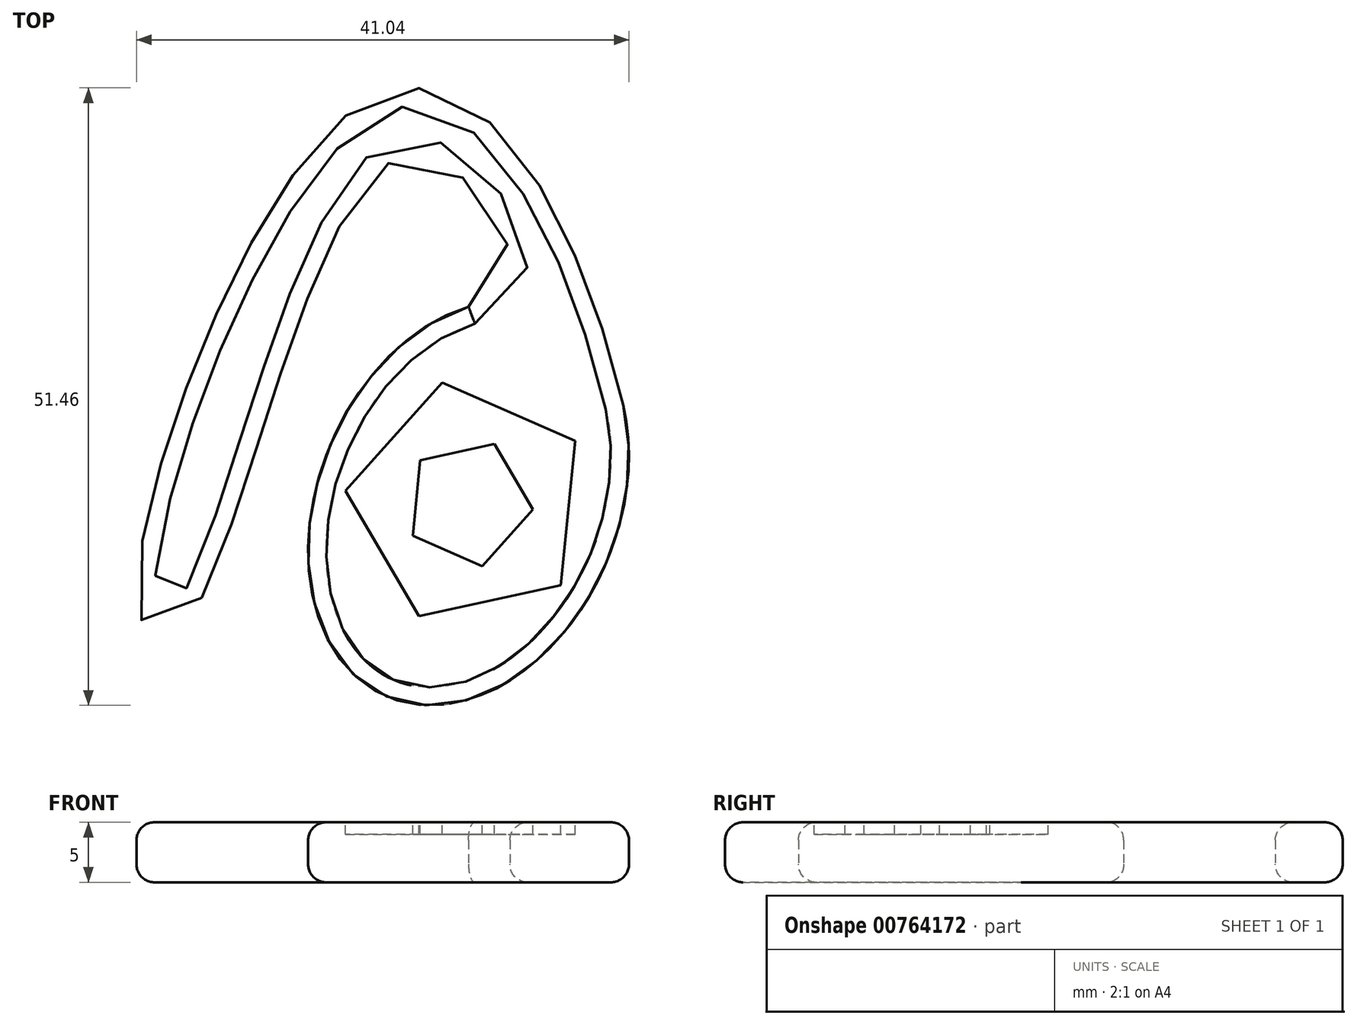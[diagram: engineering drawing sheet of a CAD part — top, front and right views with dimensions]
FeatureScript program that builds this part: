
annotation { "Feature Type Name" : "Feature", "Feature Type Description" : "" }
export const myFeature = defineFeature(function(context is Context, id is Id, definition is map)
    precondition{}
    {
        {
            var Q0;
            Q0=qCreatedBy(makeId("Top.planeOp"),FACE);
            var sketch = newSketch(context, id + "F0", { "sketchPlane" : qUnion([Q0])});
            skEllipticalArc(sketch, "E0", {});
            skFitSpline(sketch, "E1", {"points": [v(12.9, 8.18) * mm, v(-8.55, 33.47) * mm, v(-27.6, -8.45) * mm, v(-25.46, -10.73) * mm, v(-21.4, -6.17) * mm, v(-6.08, 28.66) * mm, v(2.72, 22.87) * mm, v(0, 16.37) * mm], "startDerivative": vector(-67.06, 279.77) * mm, "endDerivative": vector(-125.4, -58.98) * mm});
            skPoint(sketch, "E2", {"position": v(-6.23, -16.34) * mm});
            const initialGuessF0  = {"E0": [0, 0, -0.3861526562087075, -0.922434889898989, 0.0175, 0.0125, 3.6717083934877235, 2.3682495128656664]};
            skSetInitialGuess(sketch, initialGuessF0);
            skSolve(sketch);
        }
        {
            var Q0;
            Q0=makeQuery(id+"F0.imprint","IMPRINT",FACE,{"disambiguationData":[TD([[makeQuery(id+"F0.imprint","IMPRINT",EDGE,{"derivedFrom":sQuery(id+"F0.wireOp",EDGE,"E0")}),1.0]])]});
            extrude(context, id + "F1", {"entities" : qUnion([Q0]), "depth" : 5 * mm, "offsetDistance" : 25 * mm});
        }
        {
            var Q0;
            Q0=makeQuery(id+"F1.opExtrude","CAP_EDGE",EDGE,{"disambiguationData":[OSD([sQuery(id+"F0.wireOp",EDGE,"E1")])],"isStart":false});
            var Q1;
            Q1=makeQuery(id+"F1.opExtrude","CAP_EDGE",EDGE,{"disambiguationData":[OSD([sQuery(id+"F0.wireOp",EDGE,"E1")])],"isStart":true});
            fillet(context, id + "F2", {"entities" : qUnion([Q0, Q1]), "radius" : 1.5 * mm, "tangentPropagation" : true, "allowEdgeOverflow" : false});
        }
        {
            var Q0;
            Q0=makeQuery(id+"F1.opExtrude","CAP_FACE",FACE,{"disambiguationData":[OSD([sQuery(id+"F0.wireOp",EDGE,"E0"),sQuery(id+"F0.wireOp",EDGE,"E1")])],"isStart":false});
            var sketch = newSketch(context, id + "F3", { "sketchPlane" : qUnion([Q0])});
            skCircle(sketch, "E3.cCircle", {"center": v(0, 0) * mm, "radius": 8.33 * mm, "construction": true});
            skLineSegment(sketch, "E3.0", {"start": v(-10.25, 1.02) * mm, "end": v(-2.2, 10.06) * mm});
            skLineSegment(sketch, "E3.1", {"start": v(-2.2, 10.06) * mm, "end": v(8.89, 5.2) * mm});
            skLineSegment(sketch, "E3.2", {"start": v(8.89, 5.2) * mm, "end": v(7.7, -6.85) * mm});
            skLineSegment(sketch, "E3.3", {"start": v(7.7, -6.85) * mm, "end": v(-4.13, -9.43) * mm});
            skLineSegment(sketch, "E3.4", {"start": v(-4.13, -9.43) * mm, "end": v(-10.25, 1.02) * mm});
            skPoint(sketch, "E3.0.midPoint", {"position": v(-6.22, 5.54) * mm});
            skCircle(sketch, "E4.cCircle", {"center": v(0, 0) * mm, "radius": 4.36 * mm, "construction": true});
            skLineSegment(sketch, "E4.0", {"start": v(1.15, -5.26) * mm, "end": v(-4.65, -2.72) * mm});
            skLineSegment(sketch, "E4.1", {"start": v(-4.65, -2.72) * mm, "end": v(-4.02, 3.58) * mm});
            skLineSegment(sketch, "E4.2", {"start": v(-4.02, 3.58) * mm, "end": v(2.16, 4.93) * mm});
            skLineSegment(sketch, "E4.3", {"start": v(2.16, 4.93) * mm, "end": v(5.36, -0.53) * mm});
            skLineSegment(sketch, "E4.4", {"start": v(5.36, -0.53) * mm, "end": v(1.15, -5.26) * mm});
            skPoint(sketch, "E4.0.midPoint", {"position": v(-1.75, -3.99) * mm});
            skLineSegment(sketch, "E5", {"start": v(-4.13, -9.43) * mm, "end": v(2.16, 4.93) * mm, "construction": true});
            skSolve(sketch);
        }
        {
            var Q0;
            Q0=makeQuery(id+"F3.imprint","IMPRINT",FACE,{"disambiguationData":[TD([[makeQuery(id+"F3.imprint","IMPRINT",EDGE,{"derivedFrom":sQuery(id+"F3.wireOp",EDGE,"E3.0")}),-1.0]])]});
            extrude(context, id + "F4", {"entities" : qUnion([Q0]), "operationType" : NewBodyOperationType.REMOVE, "oppositeDirection" : true, "depth" : 1 * mm, "offsetDistance" : 25 * mm});
        }
    });
